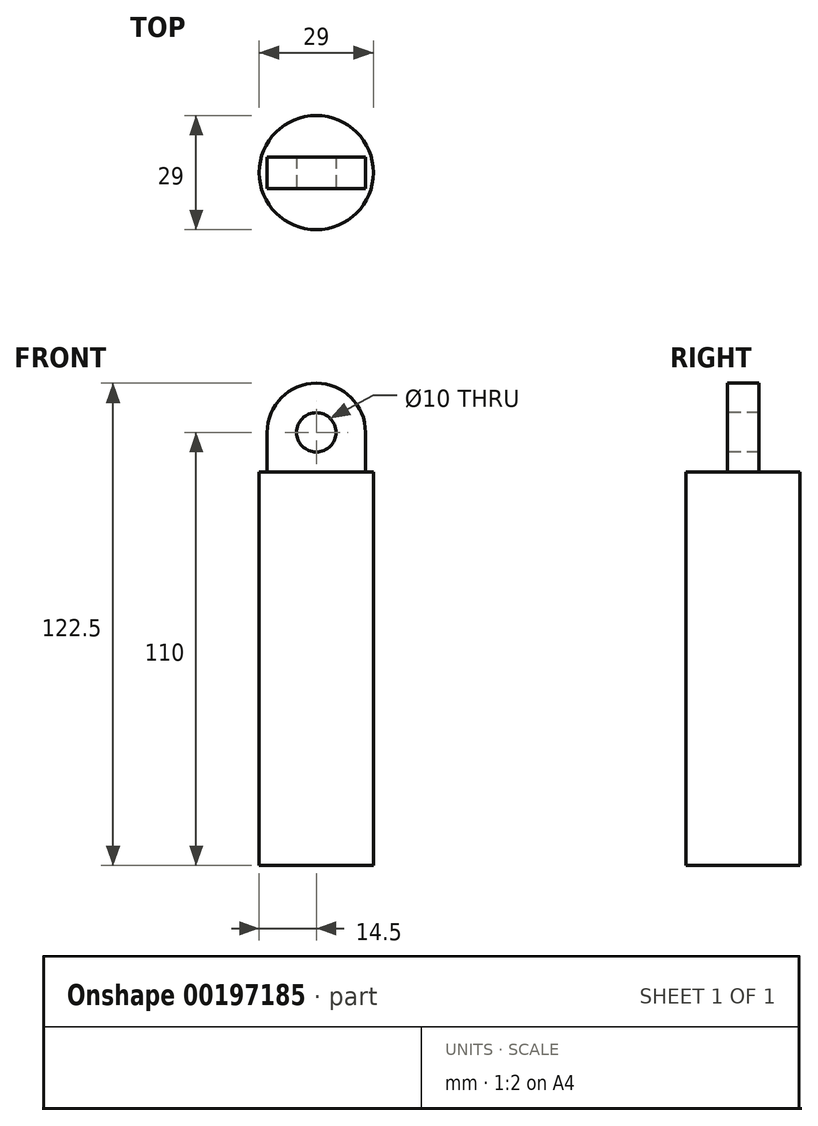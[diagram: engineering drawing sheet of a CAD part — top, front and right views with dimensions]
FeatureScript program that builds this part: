
annotation { "Feature Type Name" : "Feature", "Feature Type Description" : "" }
export const myFeature = defineFeature(function(context is Context, id is Id, definition is map)
    precondition{}
    {
        {
            var Q0;
            Q0=qCreatedBy(makeId("Top.planeOp"),FACE);
            var sketch = newSketch(context, id + "F0", { "sketchPlane" : qUnion([Q0])});
            skCircle(sketch, "E0", {"center": v(0, 0) * mm, "radius": 14.5 * mm});
            skSolve(sketch);
        }
        {
            var Q0;
            Q0 = qSketchRegion(id + "F0", true);
            extrude(context, id + "F1", {"entities" : qUnion([Q0]), "endBound" : BoundingType.SYMMETRIC, "depth" : 100 * mm});
        }
        {
            var Q0;
            Q0=makeQuery(id+"F1.opExtrude","CAP_FACE",FACE,{"disambiguationData":[OSD([sQuery(id+"F0.wireOp",EDGE,"E0")])],"isStart":false});
            var sketch = newSketch(context, id + "F2", { "sketchPlane" : qUnion([Q0])});
            skLineSegment(sketch, "E1.bottom", {"start": v(-12.5, 4) * mm, "end": v(12.5, 4) * mm});
            skLineSegment(sketch, "E1.top", {"start": v(-12.5, -4) * mm, "end": v(12.5, -4) * mm});
            skLineSegment(sketch, "E1.left", {"start": v(-12.5, 4) * mm, "end": v(-12.5, -4) * mm});
            skLineSegment(sketch, "E1.right", {"start": v(12.5, 4) * mm, "end": v(12.5, -4) * mm});
            skPoint(sketch, "E1.middle", {"position": v(0, 0) * mm});
            skSolve(sketch);
        }
        {
            var Q0;
            Q0 = qSketchRegion(id + "F2", true);
            extrude(context, id + "F3", {"entities" : qUnion([Q0]), "operationType" : NewBodyOperationType.ADD, "depth" : 10 * mm});
        }
        {
            var Q0;
            Q0=makeQuery(id+"F3.opExtrude","SWEPT_FACE",FACE,{"disambiguationData":[OSD([sQuery(id+"F2.wireOp",EDGE,"E1.top")])]});
            var sketch = newSketch(context, id + "F4", { "sketchPlane" : qUnion([Q0])});
            skArc(sketch, "E2", {"start": v(12.5, 60) * mm, "mid": v(0, 72.5) * mm, "end": v(-12.5, 60) * mm});
            skLineSegment(sketch, "E3", {"start": v(-12.5, 60) * mm, "end": v(12.5, 60) * mm});
            skSolve(sketch);
        }
        {
            var Q0;
            Q0 = qSketchRegion(id + "F4", true);
            extrude(context, id + "F5", {"entities" : qUnion([Q0]), "operationType" : NewBodyOperationType.ADD, "oppositeDirection" : true, "depth" : 8 * mm});
        }
        {
            var Q0;
            Q0=makeQuery(id+"F5.boolean.opBoolean","MERGE",FACE,{"derivedFrom":[makeQuery(id+"F3.opExtrude","SWEPT_FACE",FACE,{"disambiguationData":[OSD([sQuery(id+"F2.wireOp",EDGE,"E1.top")])]}),makeQuery(id+"F5.opExtrude","CAP_FACE",FACE,{"disambiguationData":[OSD([sQuery(id+"F4.wireOp",EDGE,"E2"),sQuery(id+"F4.wireOp",EDGE,"E3")])],"isStart":true})]});
            var sketch = newSketch(context, id + "F6", { "sketchPlane" : qUnion([Q0])});
            skLineSegment(sketch, "E4", {"start": v(-12.5, 60) * mm, "end": v(12.5, 60) * mm, "construction": true});
            skCircle(sketch, "E5", {"center": v(0, 60) * mm, "radius": 5 * mm});
            skSolve(sketch);
        }
        {
            var Q0;
            Q0 = qSketchRegion(id + "F6", true);
            extrude(context, id + "F7", {"entities" : qUnion([Q0]), "operationType" : NewBodyOperationType.REMOVE, "oppositeDirection" : true, "depth" : 25 * mm});
        }
    });
